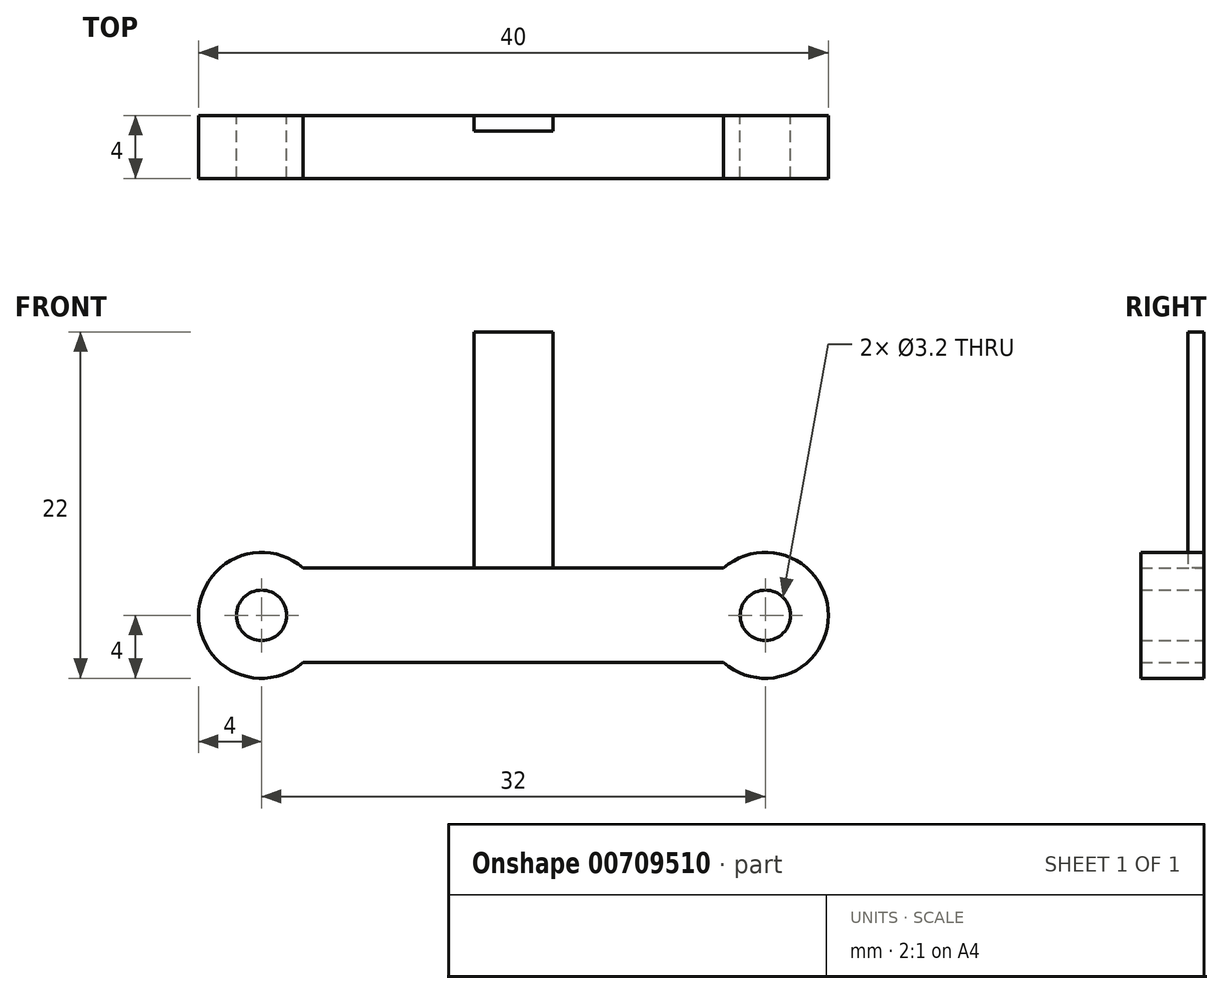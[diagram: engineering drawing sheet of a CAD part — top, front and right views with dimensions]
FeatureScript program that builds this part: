
annotation { "Feature Type Name" : "Feature", "Feature Type Description" : "" }
export const myFeature = defineFeature(function(context is Context, id is Id, definition is map)
    precondition{}
    {
        {
            var Q0;
            Q0=qCreatedBy(makeId("Front.planeOp"),FACE);
            var sketch = newSketch(context, id + "F0", { "sketchPlane" : qUnion([Q0])});
            skCircle(sketch, "E0", {"center": v(-16, 0) * mm, "radius": 1.6 * mm});
            skCircle(sketch, "E1", {"center": v(16, 0) * mm, "radius": 1.6 * mm});
            skLineSegment(sketch, "E2", {"start": v(-16, 0) * mm, "end": v(16, 0) * mm, "construction": true});
            skPoint(sketch, "E3.start.orphan", {"position": v(0, 0) * mm});
            skArc(sketch, "E4", {"start": v(13.35, -3) * mm, "mid": v(20, 0) * mm, "end": v(13.35, 3) * mm});
            skArc(sketch, "E5", {"start": v(-13.35, 3) * mm, "mid": v(-20, 0) * mm, "end": v(-13.35, -3) * mm});
            skLineSegment(sketch, "E6.bottom", {"start": v(-13.35, 3) * mm, "end": v(13.35, 3) * mm});
            skLineSegment(sketch, "E6.top", {"start": v(-13.35, -3) * mm, "end": v(13.35, -3) * mm});
            skSolve(sketch);
        }
        {
            var Q0;
            Q0=makeQuery(id+"F0.imprint","IMPRINT",FACE,{"disambiguationData":[TD([[makeQuery(id+"F0.imprint","IMPRINT",EDGE,{"derivedFrom":sQuery(id+"F0.wireOp",EDGE,"E0")}),-1.0]])]});
            extrude(context, id + "F1", {"entities" : qUnion([Q0]), "depth" : 4 * mm, "offsetDistance" : 25 * mm});
        }
        {
            var Q0;
            Q0=makeQuery(id+"F1.opExtrude","SWEPT_FACE",FACE,{"disambiguationData":[OSD([sQuery(id+"F0.wireOp",EDGE,"E6.bottom")])]});
            var sketch = newSketch(context, id + "F2", { "sketchPlane" : qUnion([Q0])});
            skLineSegment(sketch, "E7", {"start": v(0, 0) * mm, "end": v(0, 9.52) * mm, "construction": true});
            skLineSegment(sketch, "E8.bottom", {"start": v(-2.5, 0) * mm, "end": v(2.5, 0) * mm});
            skLineSegment(sketch, "E8.top", {"start": v(-2.5, -1) * mm, "end": v(2.5, -1) * mm});
            skLineSegment(sketch, "E8.left", {"start": v(-2.5, 0) * mm, "end": v(-2.5, -1) * mm});
            skLineSegment(sketch, "E8.right", {"start": v(2.5, 0) * mm, "end": v(2.5, -1) * mm});
            skSolve(sketch);
        }
        {
            var Q0;
            Q0=makeQuery(id+"F2.imprint","IMPRINT",FACE,{"disambiguationData":[TD([[makeQuery(id+"F2.imprint","IMPRINT",EDGE,{"derivedFrom":sQuery(id+"F2.wireOp",EDGE,"E8.bottom")}),-1.0]])]});
            extrude(context, id + "F3", {"entities" : qUnion([Q0]), "operationType" : NewBodyOperationType.ADD, "depth" : 15 * mm, "offsetDistance" : 25 * mm});
        }
    });
